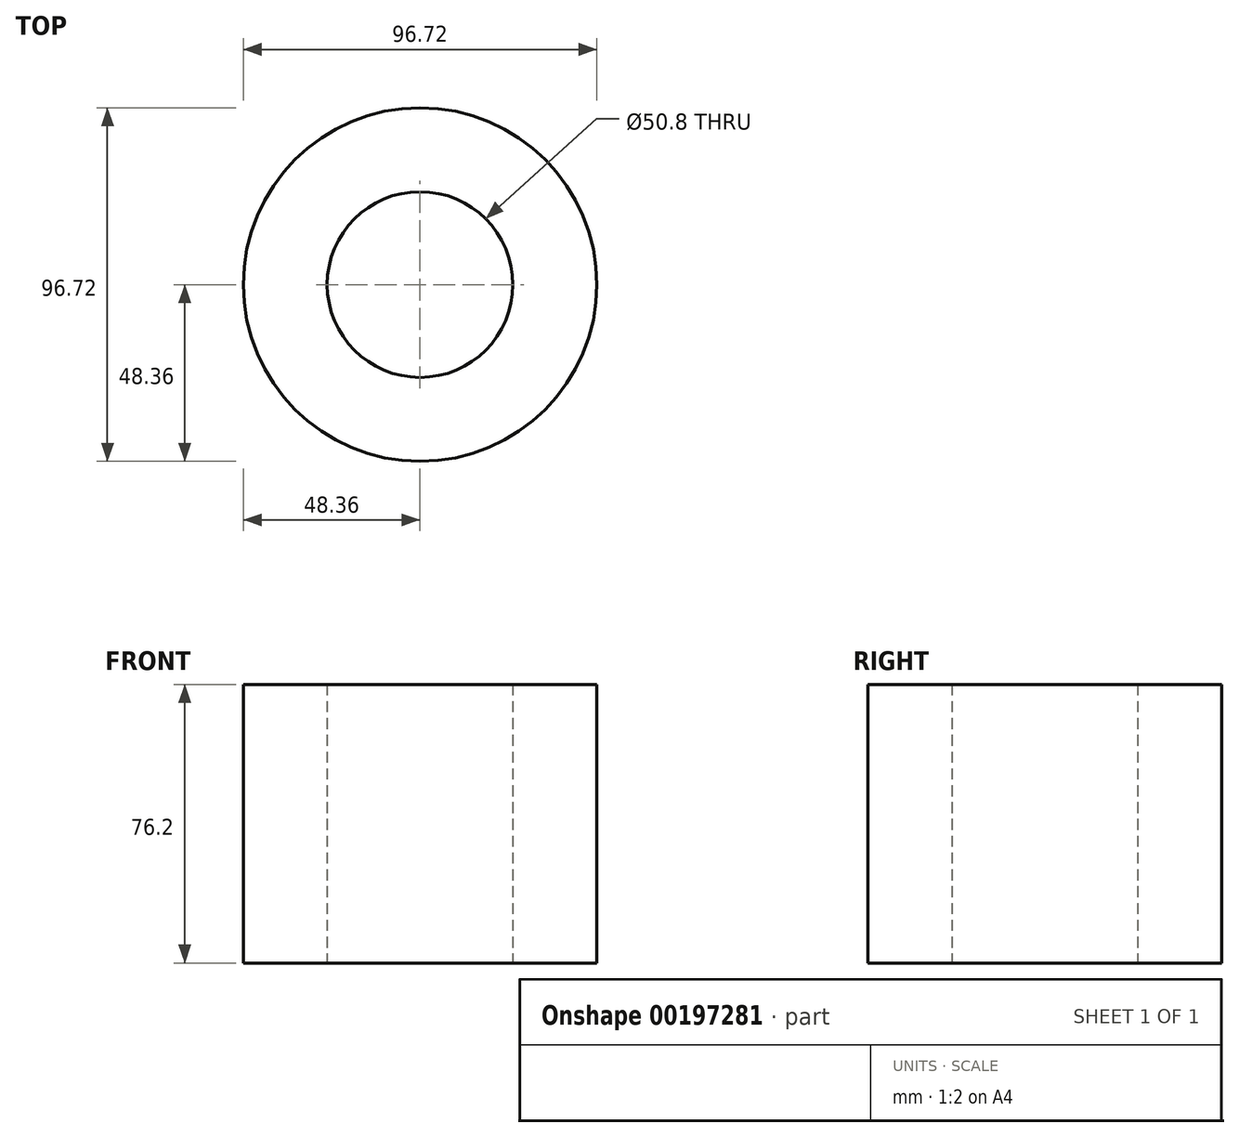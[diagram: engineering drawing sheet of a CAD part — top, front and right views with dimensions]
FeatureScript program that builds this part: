
annotation { "Feature Type Name" : "Feature", "Feature Type Description" : "" }
export const myFeature = defineFeature(function(context is Context, id is Id, definition is map)
    precondition{}
    {
        {
            var Q0;
            Q0=qCreatedBy(makeId("Top.planeOp"),FACE);
            var sketch = newSketch(context, id + "F0", { "sketchPlane" : qUnion([Q0])});
            skCircle(sketch, "E0", {"center": v(0, 0) * mm, "radius": 48.36 * mm});
            skCircle(sketch, "E1", {"center": v(0, 0) * mm, "radius": 25.4 * mm});
            skSolve(sketch);
        }
        {
            var Q0;
            Q0=makeQuery(id+"F0.imprint","IMPRINT",FACE,{"disambiguationData":[TD([[makeQuery(id+"F0.imprint","IMPRINT",EDGE,{"derivedFrom":sQuery(id+"F0.wireOp",EDGE,"E0")}),1.0]])]});
            extrude(context, id + "F1", {"entities" : qUnion([Q0]), "depth" : 76.2 * mm});
        }
    });
